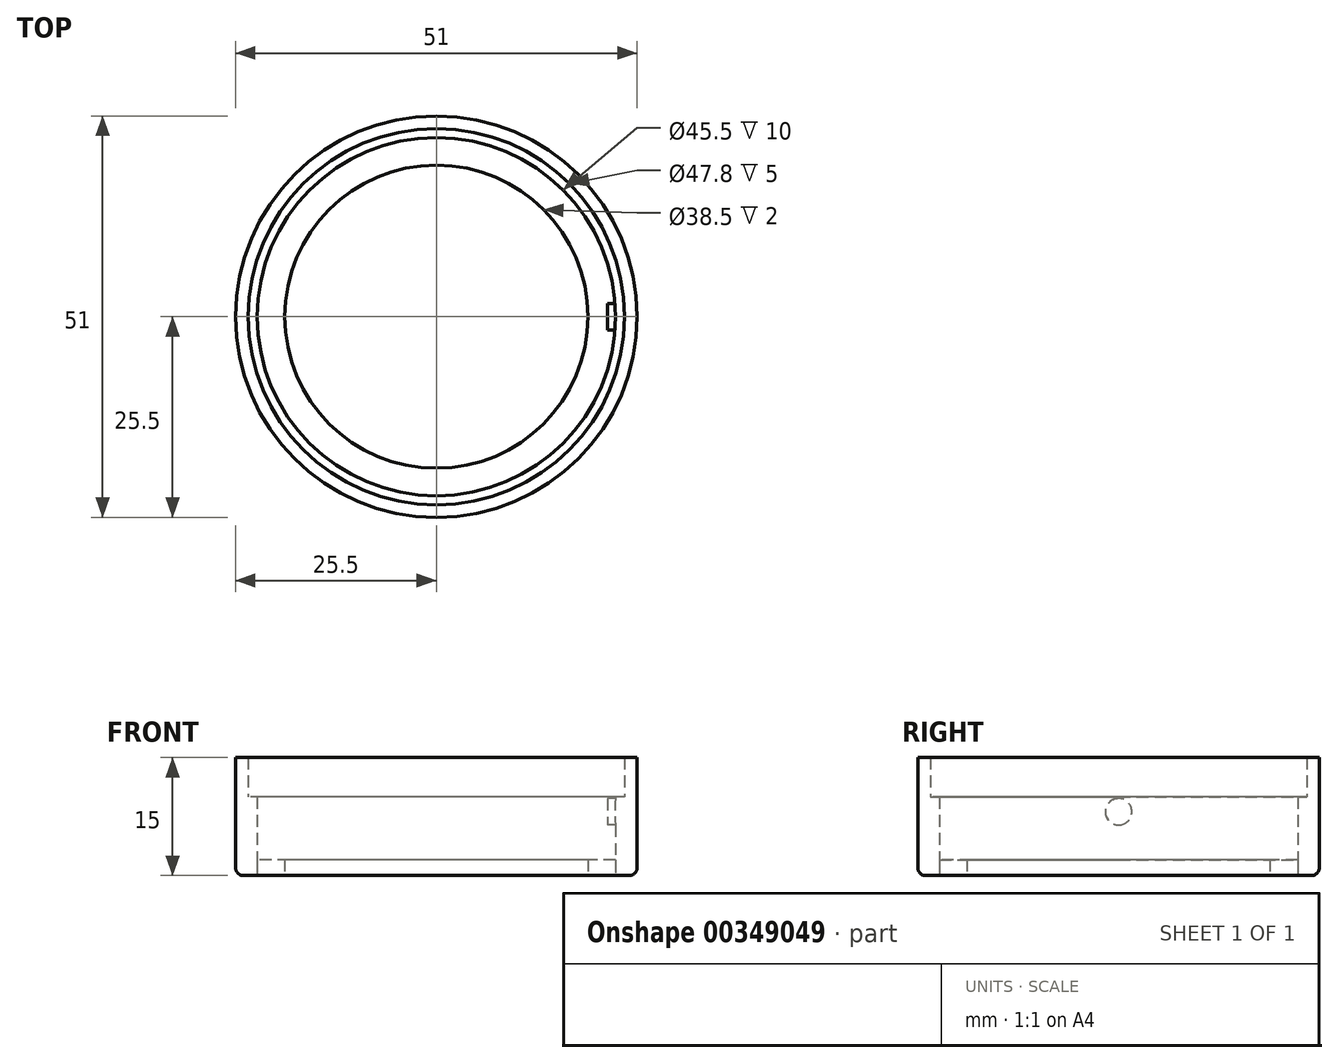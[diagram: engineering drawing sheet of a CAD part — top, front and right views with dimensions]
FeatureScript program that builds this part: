
annotation { "Feature Type Name" : "Feature", "Feature Type Description" : "" }
export const myFeature = defineFeature(function(context is Context, id is Id, definition is map)
    precondition{}
    {
        {
            var Q0;
            Q0=qCreatedBy(makeId("Top.planeOp"),FACE);
            var sketch = newSketch(context, id + "F0", { "sketchPlane" : qUnion([Q0])});
            skCircle(sketch, "E0", {"center": v(0, 0) * mm, "radius": 25.5 * mm});
            skCircle(sketch, "E1", {"center": v(0, 0) * mm, "radius": 23.9 * mm});
            skCircle(sketch, "E2", {"center": v(0, 0) * mm, "radius": 22.75 * mm});
            skCircle(sketch, "E3", {"center": v(0, 0) * mm, "radius": 19.25 * mm});
            skSolve(sketch);
        }
        {
            var Q0;
            Q0=makeQuery(id+"F0.imprint","IMPRINT",FACE,{"disambiguationData":[TD([[makeQuery(id+"F0.imprint","IMPRINT",EDGE,{"derivedFrom":sQuery(id+"F0.wireOp",EDGE,"E2")}),1.0]])]});
            extrude(context, id + "F1", {"entities" : qUnion([Q0]), "depth" : 2 * mm});
        }
        {
            var Q0;
            Q0=makeQuery(id+"F0.imprint","IMPRINT",FACE,{"disambiguationData":[TD([[makeQuery(id+"F0.imprint","IMPRINT",EDGE,{"derivedFrom":sQuery(id+"F0.wireOp",EDGE,"E1")}),1.0]])]});
            extrude(context, id + "F2", {"entities" : qUnion([Q0]), "depth" : 10 * mm});
        }
        {
            var Q0;
            Q0=makeQuery(id+"F0.imprint","IMPRINT",FACE,{"disambiguationData":[TD([[makeQuery(id+"F0.imprint","IMPRINT",EDGE,{"derivedFrom":sQuery(id+"F0.wireOp",EDGE,"E0")}),1.0]])]});
            extrude(context, id + "F3", {"entities" : qUnion([Q0]), "operationType" : NewBodyOperationType.ADD, "depth" : 15 * mm});
        }
        {
            var Q0;
            Q0=qCreatedBy(makeId("Right.planeOp"),FACE);
            cPlane(context, id + "F4", {"entities" : qUnion([Q0]), "cplaneType" : CPlaneType.OFFSET, "offset" : 21.75 * mm, "width" : 150 * mm, "height" : 150 * mm});
        }
        {
            var Q0;
            Q0=qCreatedBy(id+"F4.planeOp",FACE);
            var sketch = newSketch(context, id + "F5", { "sketchPlane" : qUnion([Q0])});
            skLineSegment(sketch, "E4", {"start": v(0, 0) * mm, "end": v(0, 1.55) * mm});
            skLineSegment(sketch, "E5", {"start": v(0, 1.55) * mm, "end": v(0, 8.1) * mm});
            skCircle(sketch, "E6", {"center": v(0, 8.1) * mm, "radius": 1.68 * mm});
            skSolve(sketch);
        }
        {
            var Q0;
            Q0=makeQuery(id+"F5.imprint","IMPRINT",FACE,{"disambiguationData":[TD([[makeQuery(id+"F5.imprint","IMPRINT",EDGE,{"derivedFrom":sQuery(id+"F5.wireOp",EDGE,"E6")}),1.0]])]});
            var Q1;
            Q1=sQuery(id+"F5.wireOp",EDGE,"E6");
            extrude(context, id + "F6", {"entities" : qUnion([Q0]), "operationType" : NewBodyOperationType.ADD, "surfaceEntities" : qUnion([Q1]), "depth" : 2 * mm});
        }
        {
            var Q0;
            Q0=makeQuery(id+"F3.opExtrude","CAP_EDGE",EDGE,{"disambiguationData":[OSD([sQuery(id+"F0.wireOp",EDGE,"E0")])],"isStart":true});
            fillet(context, id + "F7", {"entities" : qUnion([Q0]), "radius" : 1 * mm, "tangentPropagation" : true, "allowEdgeOverflow" : false});
        }
    });
